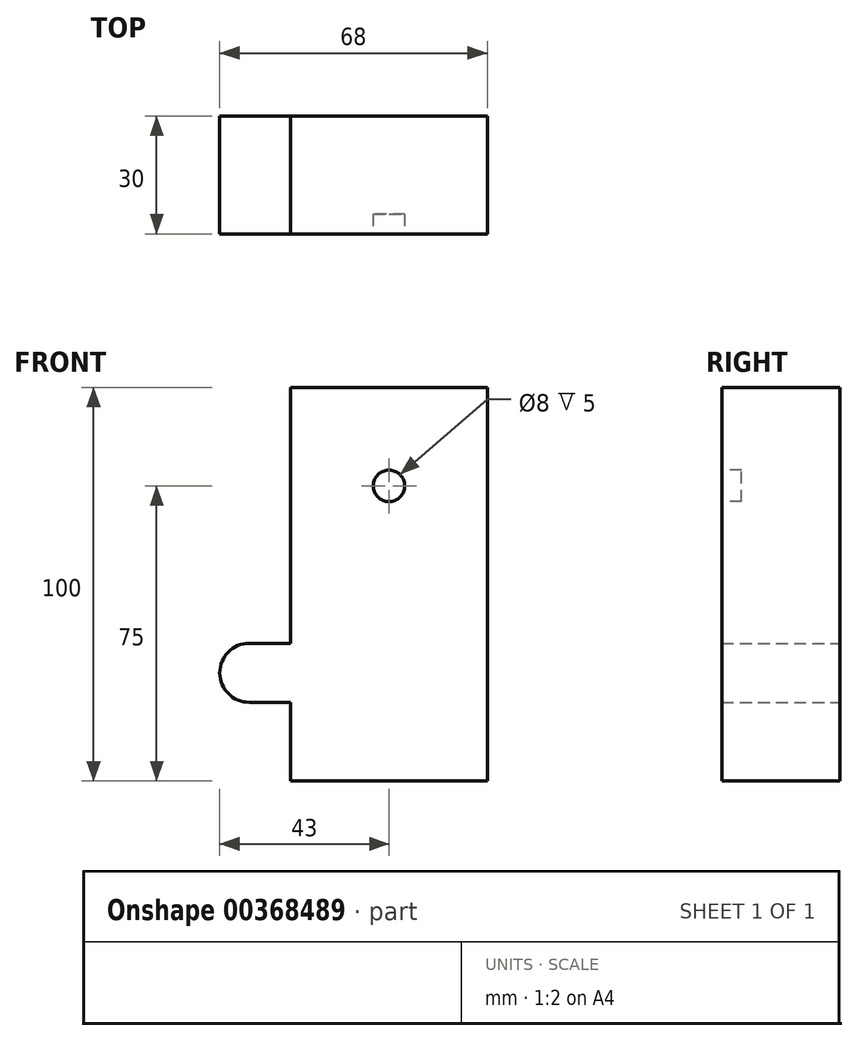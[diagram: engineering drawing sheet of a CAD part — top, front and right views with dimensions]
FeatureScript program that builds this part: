
annotation { "Feature Type Name" : "Feature", "Feature Type Description" : "" }
export const myFeature = defineFeature(function(context is Context, id is Id, definition is map)
    precondition{}
    {
        {
            var Q0;
            Q0=qCreatedBy(makeId("Front.planeOp"),FACE);
            var sketch = newSketch(context, id + "F0", { "sketchPlane" : qUnion([Q0])});
            skLineSegment(sketch, "E0.bottom", {"start": v(50, -50) * mm, "end": v(0, -50) * mm});
            skLineSegment(sketch, "E0.top", {"start": v(50, 50) * mm, "end": v(0, 50) * mm});
            skLineSegment(sketch, "E0.left", {"start": v(50, -50) * mm, "end": v(50, 50) * mm});
            skPoint(sketch, "E0.middle", {"position": v(0, 0) * mm});
            skLineSegment(sketch, "E1", {"start": v(0, 50) * mm, "end": v(0, -15) * mm});
            skLineSegment(sketch, "E2.bottom", {"start": v(0, -15) * mm, "end": v(-10.5, -15) * mm});
            skLineSegment(sketch, "E2.top", {"start": v(0, -30) * mm, "end": v(-10.5, -30) * mm});
            skArc(sketch, "E3", {"start": v(-10.5, -15) * mm, "mid": v(-18, -22.5) * mm, "end": v(-10.5, -30) * mm});
            skPoint(sketch, "E0.right.end.orphan", {"position": v(-50, 50) * mm});
            skPoint(sketch, "E4.orphan", {"position": v(-50, -50) * mm});
            skLineSegment(sketch, "E5.trimOffspring", {"start": v(0, -30) * mm, "end": v(0, -50) * mm});
            skSolve(sketch);
        }
        {
            var Q0;
            Q0 = qSketchRegion(id + "F0", true);
            extrude(context, id + "F1", {"entities" : qUnion([Q0]), "endBound" : BoundingType.SYMMETRIC, "depth" : 30 * mm});
        }
        {
            var Q0;
            Q0=makeQuery(id+"F1.opExtrude","CAP_FACE",FACE,{"disambiguationData":[OSD([sQuery(id+"F0.wireOp",EDGE,"E0.bottom"),sQuery(id+"F0.wireOp",EDGE,"E0.top"),sQuery(id+"F0.wireOp",EDGE,"E0.left"),sQuery(id+"F0.wireOp",EDGE,"E1"),sQuery(id+"F0.wireOp",EDGE,"E2.bottom"),sQuery(id+"F0.wireOp",EDGE,"E2.top"),sQuery(id+"F0.wireOp",EDGE,"E3"),sQuery(id+"F0.wireOp",EDGE,"E5.trimOffspring")])],"isStart":false});
            var sketch = newSketch(context, id + "F2", { "sketchPlane" : qUnion([Q0])});
            skCircle(sketch, "E6", {"center": v(25, 25) * mm, "radius": 4 * mm});
            skSolve(sketch);
        }
        {
            var Q0;
            Q0 = qSketchRegion(id + "F2", true);
            extrude(context, id + "F3", {"entities" : qUnion([Q0]), "operationType" : NewBodyOperationType.REMOVE, "oppositeDirection" : true, "depth" : 5 * mm});
        }
    });
